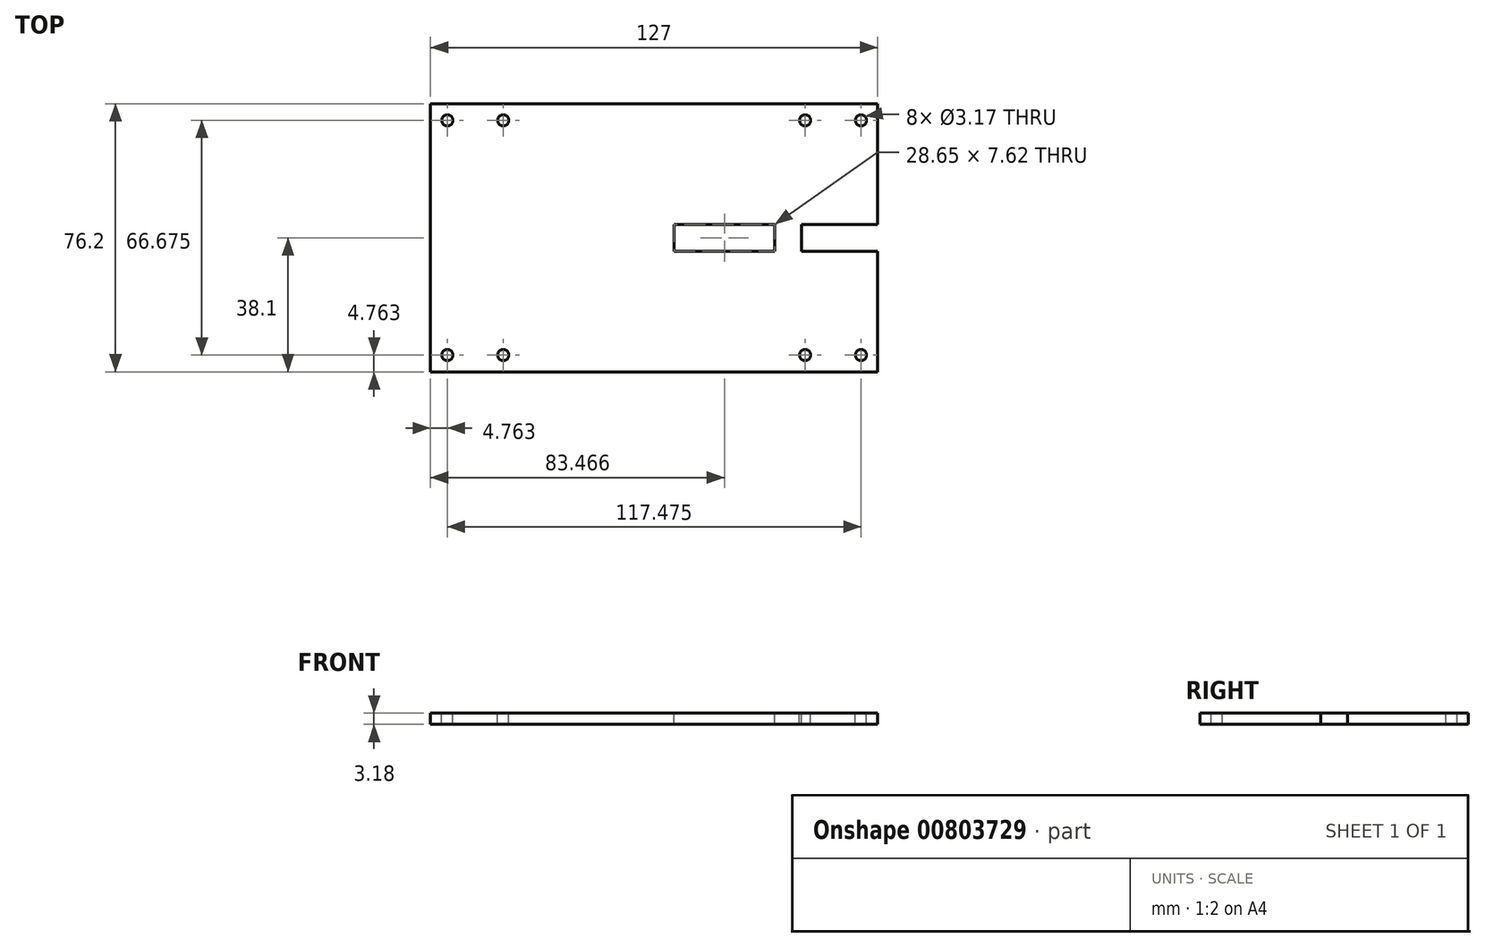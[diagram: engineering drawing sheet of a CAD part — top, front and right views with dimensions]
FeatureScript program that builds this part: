
annotation { "Feature Type Name" : "Feature", "Feature Type Description" : "" }
export const myFeature = defineFeature(function(context is Context, id is Id, definition is map)
    precondition{}
    {
        {
            var Q0;
            Q0=qCreatedBy(makeId("Top.planeOp"),FACE);
            var sketch = newSketch(context, id + "F0", { "sketchPlane" : qUnion([Q0])});
            skLineSegment(sketch, "E0.bottom", {"start": v(0, 0) * mm, "end": v(127, 0) * mm});
            skLineSegment(sketch, "E0.top", {"start": v(0, 76.2) * mm, "end": v(127, 76.2) * mm});
            skLineSegment(sketch, "E0.left", {"start": v(0, 0) * mm, "end": v(0, 76.2) * mm});
            skLineSegment(sketch, "E1.bottom", {"start": v(127, 41.91) * mm, "end": v(105.4, 41.91) * mm});
            skLineSegment(sketch, "E1.top", {"start": v(127, 34.3) * mm, "end": v(105.4, 34.3) * mm});
            skLineSegment(sketch, "E2", {"start": v(127, 76.2) * mm, "end": v(127, 41.91) * mm});
            skLineSegment(sketch, "E3", {"start": v(127, 34.3) * mm, "end": v(127, 0) * mm});
            skCircle(sketch, "E4", {"center": v(122.24, 71.44) * mm, "radius": 1.59 * mm});
            skCircle(sketch, "E5", {"center": v(106.36, 71.44) * mm, "radius": 1.59 * mm});
            skLineSegment(sketch, "E6", {"start": v(122.24, 71.44) * mm, "end": v(106.36, 71.44) * mm});
            skCircle(sketch, "E7", {"center": v(122.24, 4.76) * mm, "radius": 1.59 * mm});
            skCircle(sketch, "E8", {"center": v(106.36, 4.76) * mm, "radius": 1.59 * mm});
            skLineSegment(sketch, "E9", {"start": v(122.24, 4.76) * mm, "end": v(106.36, 4.76) * mm});
            skLineSegment(sketch, "E10", {"start": v(114.3, 71.44) * mm, "end": v(114.3, 76.2) * mm});
            skLineSegment(sketch, "E11", {"start": v(114.3, 4.76) * mm, "end": v(114.3, 0) * mm});
            skLineSegment(sketch, "E12", {"start": v(122.24, 4.76) * mm, "end": v(127, 4.76) * mm});
            skLineSegment(sketch, "E13", {"start": v(122.24, 71.44) * mm, "end": v(127, 71.44) * mm});
            skLineSegment(sketch, "E14.left", {"start": v(105.4, 41.91) * mm, "end": v(105.4, 34.3) * mm});
            skLineSegment(sketch, "E14.right", {"start": v(69.14, 41.91) * mm, "end": v(69.14, 34.3) * mm});
            skLineSegment(sketch, "E15", {"start": v(97.8, 41.91) * mm, "end": v(97.8, 34.3) * mm});
            skLineSegment(sketch, "E16", {"start": v(69.14, 41.91) * mm, "end": v(97.8, 41.91) * mm});
            skLineSegment(sketch, "E17", {"start": v(97.8, 34.3) * mm, "end": v(69.14, 34.3) * mm});
            skLineSegment(sketch, "E18", {"start": v(97.8, 34.3) * mm, "end": v(105.4, 34.3) * mm});
            skCircle(sketch, "E19", {"center": v(20.64, 4.76) * mm, "radius": 1.59 * mm});
            skCircle(sketch, "E20", {"center": v(4.76, 4.76) * mm, "radius": 1.59 * mm});
            skLineSegment(sketch, "E21", {"start": v(20.64, 4.76) * mm, "end": v(4.76, 4.76) * mm});
            skLineSegment(sketch, "E22", {"start": v(12.7, 4.76) * mm, "end": v(12.7, 0) * mm});
            skCircle(sketch, "E23", {"center": v(20.64, 71.44) * mm, "radius": 1.59 * mm});
            skCircle(sketch, "E24", {"center": v(4.76, 71.44) * mm, "radius": 1.59 * mm});
            skLineSegment(sketch, "E25", {"start": v(20.64, 71.44) * mm, "end": v(4.76, 71.44) * mm});
            skLineSegment(sketch, "E26", {"start": v(12.7, 71.44) * mm, "end": v(12.7, 76.2) * mm});
            skSolve(sketch);
        }
        {
            var Q0;
            Q0 = qSketchRegion(id + "F0", true);
            extrude(context, id + "F1", {"entities" : qUnion([Q0]), "oppositeDirection" : true, "depth" : 3.17 * mm, "offsetDistance" : 25.4 * mm});
        }
    });
